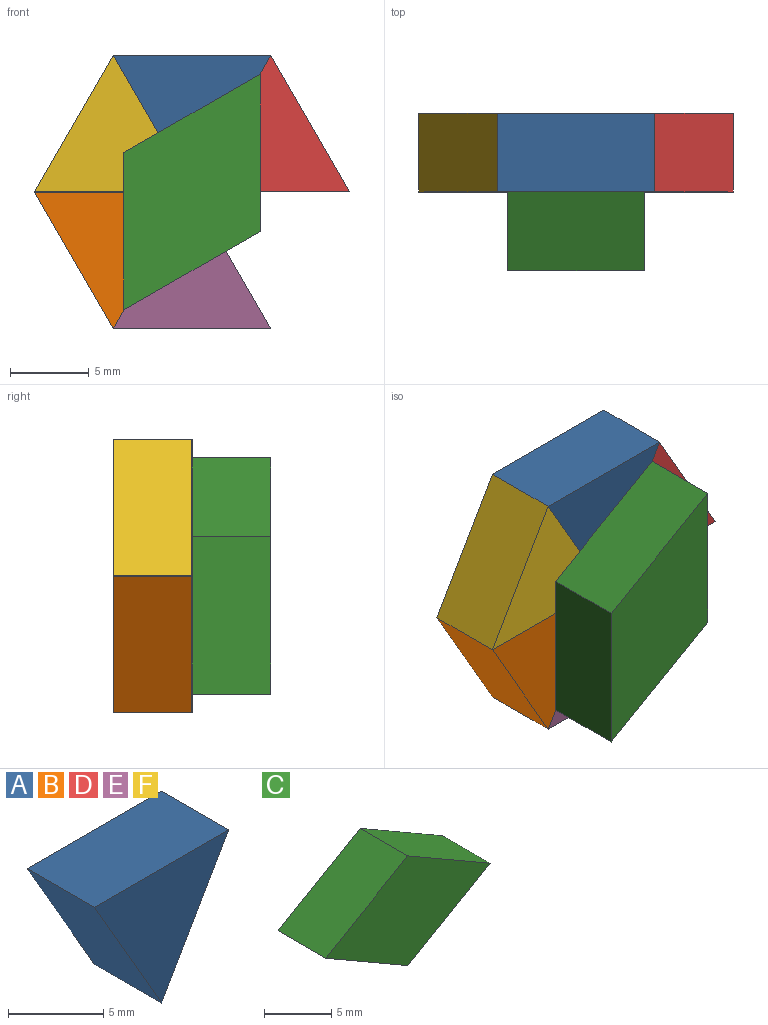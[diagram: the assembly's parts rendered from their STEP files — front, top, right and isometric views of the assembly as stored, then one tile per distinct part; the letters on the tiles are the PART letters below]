
ASSEMBLY  parts=6 mates=5
PART A: 5 faces, bbox 10x5x8.7 mm
  f0: plane 8.66x5mm, normal (-0.87,0,-0.5), area 50mm2, adj f1,f2,f3,f4
  f1: plane 8.66x5mm, normal (0.87,0,-0.5), area 50mm2, adj f0,f2,f3,f4
  f2: plane 10x5mm, normal (0,0,1), area 50mm2, adj f0,f1,f3,f4
  f3: plane 10x8.66mm, normal (0,-1,0), area 43.3mm2, adj f0,f1,f2
  f4: plane 10x8.66mm, normal (0,1,0), area 43.3mm2, adj f0,f1,f2
PART B: same geometry as A
PART C: 6 faces, bbox 17.3x5x10 mm
  f0: plane 8.66x5mm, normal (-0.5,0,-0.87), area 50mm2, adj f1,f3,f4,f5
  f1: plane 8.66x5mm, normal (0.5,0,-0.87), area 50mm2, adj f0,f2,f4,f5
  f2: plane 8.66x5mm, normal (0.5,0,0.87), area 50mm2, adj f1,f3,f4,f5
  f3: plane 8.66x5mm, normal (-0.5,0,0.87), area 50mm2, adj f0,f2,f4,f5
  f4: plane 17.32x10mm, normal (0,-1,0), area 86.6mm2, adj f0,f1,f2,f3
  f5: plane 17.32x10mm, normal (0,1,0), area 86.6mm2, adj f0,f1,f2,f3
PART D: same geometry as A
PART E: same geometry as A
PART F: same geometry as A
PLACE A rot(axis=(0.87,0,-0.5),180deg) t=(-27.88,-22.04,-32.51)mm
PLACE B t=(0.92,-17.04,17.38)mm
PLACE C rot(axis=(0.87,0,0.5),180deg) t=(1.24,-27.04,-34.19)mm
PLACE D rot(axis=(0,-1,0),60deg) t=(-22.88,-17.04,32.75)mm
PLACE E rot(axis=(0,1,0),60deg) t=(14.51,-17.04,-19.58)mm
PLACE F rot(axis=(1,0,0),180deg) t=(0.92,-22.04,-25.8)mm
MATE fastened A.f2 <-> F.f1  axis (-0.87,0,-0.5) through (-21.79,-19.54,0.12)mm
MATE fastened E.f0 <-> B.f1  axis (-0.87,0,0.5) through (-21.79,-19.54,-8.54)mm
MATE fastened F.f2 <-> B.f2  axis (0,0,-1) through (-24.29,-19.54,-4.21)mm
MATE fastened D.f2 <-> A.f1  axis (-0.87,0,0.5) through (-16.79,-19.54,0.12)mm
MATE revolute C.f4 <-> B.f3  axis (0,1,0) through (-19.29,-22.04,-4.21)mm
